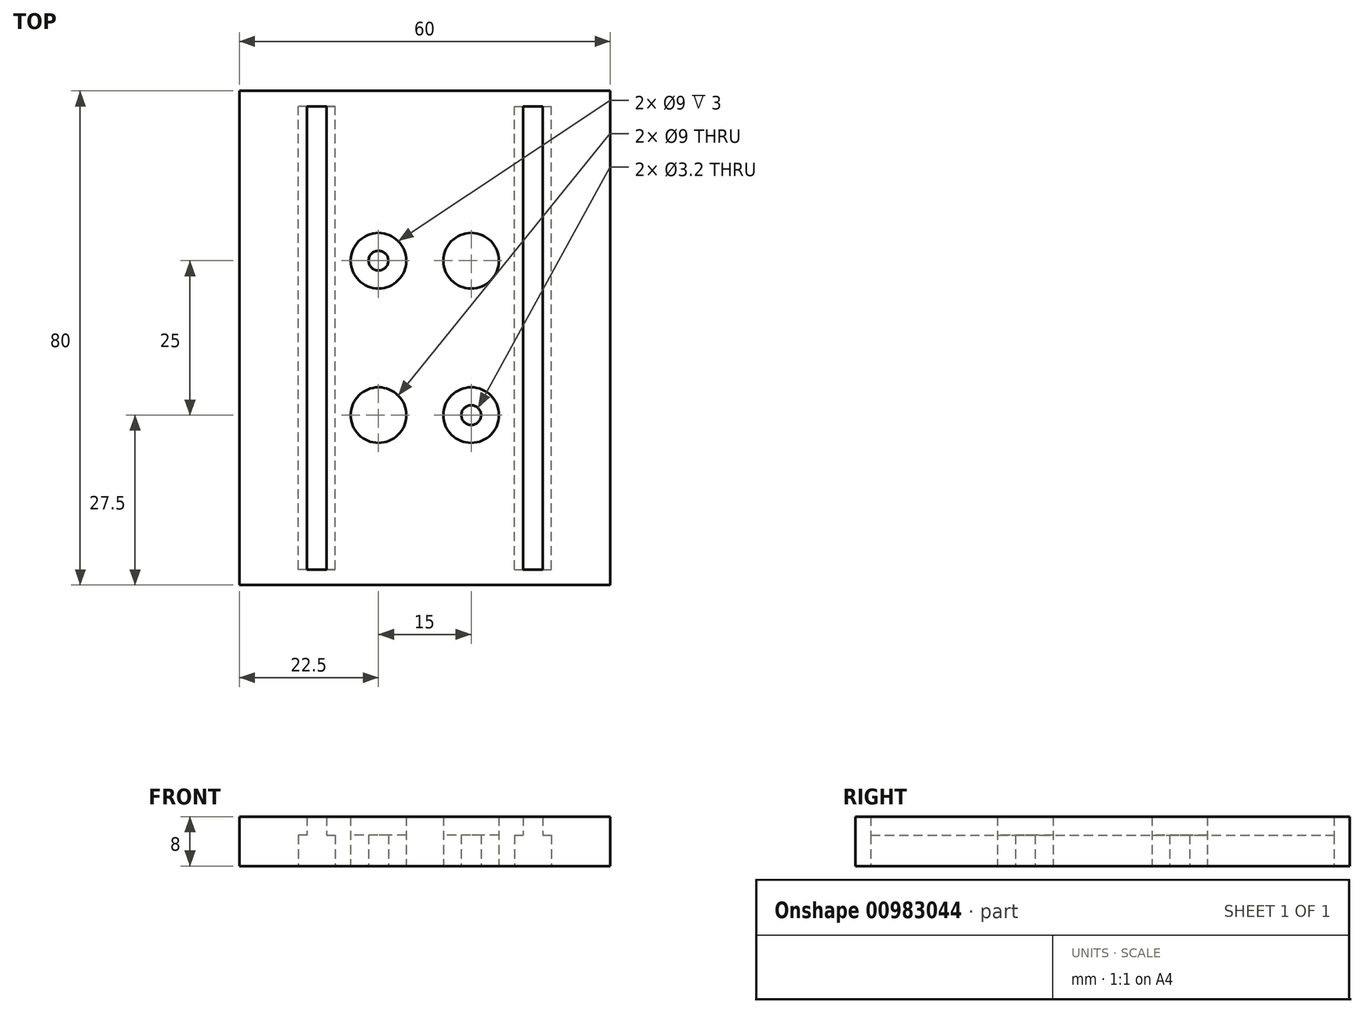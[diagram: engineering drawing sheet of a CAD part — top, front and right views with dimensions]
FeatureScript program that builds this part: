
annotation { "Feature Type Name" : "Feature", "Feature Type Description" : "" }
export const myFeature = defineFeature(function(context is Context, id is Id, definition is map)
    precondition{}
    {
        {
            var Q0;
            Q0=qCreatedBy(makeId("Top.planeOp"),FACE);
            var sketch = newSketch(context, id + "F0", { "sketchPlane" : qUnion([Q0])});
            skLineSegment(sketch, "E0.bottom", {"start": v(-30, 40) * mm, "end": v(30, 40) * mm});
            skLineSegment(sketch, "E0.top", {"start": v(-30, -40) * mm, "end": v(30, -40) * mm});
            skLineSegment(sketch, "E0.left", {"start": v(-30, 40) * mm, "end": v(-30, -40) * mm});
            skLineSegment(sketch, "E0.right", {"start": v(30, 40) * mm, "end": v(30, -40) * mm});
            skPoint(sketch, "E0.middle", {"position": v(0, 0) * mm});
            skLineSegment(sketch, "E1.bottom", {"start": v(-7.5, 12.5) * mm, "end": v(7.5, 12.5) * mm, "construction": true});
            skLineSegment(sketch, "E1.top", {"start": v(-7.5, -12.5) * mm, "end": v(7.5, -12.5) * mm, "construction": true});
            skLineSegment(sketch, "E1.left", {"start": v(-7.5, 12.5) * mm, "end": v(-7.5, -12.5) * mm, "construction": true});
            skLineSegment(sketch, "E1.right", {"start": v(7.5, 12.5) * mm, "end": v(7.5, -12.5) * mm, "construction": true});
            skCircle(sketch, "E2", {"center": v(-7.5, 12.5) * mm, "radius": 4.5 * mm});
            skCircle(sketch, "E3", {"center": v(-7.5, 12.5) * mm, "radius": 1.6 * mm});
            skCircle(sketch, "E4.MirrorC", {"center": v(-7.5, -12.5) * mm, "radius": 4.5 * mm});
            skCircle(sketch, "E5.MirrorC", {"center": v(-7.5, -12.5) * mm, "radius": 1.6 * mm});
            skCircle(sketch, "E6.MirrorC", {"center": v(7.5, 12.5) * mm, "radius": 4.5 * mm});
            skCircle(sketch, "E7.MirrorC", {"center": v(7.5, 12.5) * mm, "radius": 1.6 * mm});
            skCircle(sketch, "E8.MirrorC", {"center": v(7.5, -12.5) * mm, "radius": 4.5 * mm});
            skCircle(sketch, "E9.MirrorC", {"center": v(7.5, -12.5) * mm, "radius": 1.6 * mm});
            skSolve(sketch);
        }
        {
            var Q0;
            Q0=makeQuery(id+"F0.imprint","IMPRINT",FACE,{"disambiguationData":[TD([[makeQuery(id+"F0.imprint","IMPRINT",EDGE,{"derivedFrom":sQuery(id+"F0.wireOp",EDGE,"E0.bottom")}),-1.0]])]});
            extrude(context, id + "F1", {"entities" : qUnion([Q0]), "depth" : 8 * mm, "offsetDistance" : 25 * mm});
        }
        {
            var Q0;
            Q0=makeQuery(id+"F0.imprint","IMPRINT",FACE,{"disambiguationData":[TD([[makeQuery(id+"F0.imprint","IMPRINT",EDGE,{"derivedFrom":sQuery(id+"F0.wireOp",EDGE,"E2")}),1.0]])]});
            var Q1;
            Q1=makeQuery(id+"F0.imprint","IMPRINT",FACE,{"disambiguationData":[TD([[makeQuery(id+"F0.imprint","IMPRINT",EDGE,{"derivedFrom":sQuery(id+"F0.wireOp",EDGE,"E4.MirrorC")}),-1.0]])]});
            var Q2;
            Q2=makeQuery(id+"F0.imprint","IMPRINT",FACE,{"disambiguationData":[TD([[makeQuery(id+"F0.imprint","IMPRINT",EDGE,{"derivedFrom":sQuery(id+"F0.wireOp",EDGE,"E8.MirrorC")}),1.0]])]});
            var Q3;
            Q3=makeQuery(id+"F0.imprint","IMPRINT",FACE,{"disambiguationData":[TD([[makeQuery(id+"F0.imprint","IMPRINT",EDGE,{"derivedFrom":sQuery(id+"F0.wireOp",EDGE,"E6.MirrorC")}),-1.0]])]});
            extrude(context, id + "F2", {"entities" : qUnion([Q0, Q1, Q2, Q3]), "operationType" : NewBodyOperationType.ADD, "depth" : 5 * mm, "offsetDistance" : 25 * mm});
        }
        {
            var Q0;
            {var subQ0=sQuery(id+"F0.wireOp",EDGE,"E8.MirrorC");var subQ1=sQuery(id+"F0.wireOp",EDGE,"E6.MirrorC");var subQ2=sQuery(id+"F0.wireOp",EDGE,"E4.MirrorC");var subQ3=sQuery(id+"F0.wireOp",EDGE,"E2");Q0=makeQuery(id+"F2.boolean.opBoolean","MERGE",FACE,{"derivedFrom":[makeQuery(id+"F1.opExtrude","CAP_FACE",FACE,{"disambiguationData":[OSD([sQuery(id+"F0.wireOp",EDGE,"E0.bottom"),sQuery(id+"F0.wireOp",EDGE,"E0.top"),sQuery(id+"F0.wireOp",EDGE,"E0.left"),sQuery(id+"F0.wireOp",EDGE,"E0.right"),subQ3,subQ2,subQ1,subQ0])],"isStart":true}),makeQuery(id+"F2.opExtrude","CAP_FACE",FACE,{"disambiguationData":[OSD([subQ3,sQuery(id+"F0.wireOp",EDGE,"E3")])],"isStart":true}),makeQuery(id+"F2.opExtrude","CAP_FACE",FACE,{"disambiguationData":[OSD([subQ2,sQuery(id+"F0.wireOp",EDGE,"E5.MirrorC")])],"isStart":true}),makeQuery(id+"F2.opExtrude","CAP_FACE",FACE,{"disambiguationData":[OSD([subQ1,sQuery(id+"F0.wireOp",EDGE,"E7.MirrorC")])],"isStart":true}),makeQuery(id+"F2.opExtrude","CAP_FACE",FACE,{"disambiguationData":[OSD([subQ0,sQuery(id+"F0.wireOp",EDGE,"E9.MirrorC")])],"isStart":true})]});}
            var sketch = newSketch(context, id + "F3", { "sketchPlane" : qUnion([Q0])});
            skLineSegment(sketch, "E10.bottom", {"start": v(17.5, -37.5) * mm, "end": v(-17.5, -37.5) * mm, "construction": true});
            skLineSegment(sketch, "E10.top", {"start": v(17.5, 37.5) * mm, "end": v(-17.5, 37.5) * mm, "construction": true});
            skLineSegment(sketch, "E10.left", {"start": v(17.5, -37.5) * mm, "end": v(17.5, 37.5) * mm, "construction": true});
            skLineSegment(sketch, "E10.right", {"start": v(-17.5, -37.5) * mm, "end": v(-17.5, 37.5) * mm, "construction": true});
            skPoint(sketch, "E10.middle", {"position": v(0, 0) * mm});
            skLineSegment(sketch, "E11.bottom", {"start": v(-17.5, 37.5) * mm, "end": v(-20.5, 37.5) * mm});
            skLineSegment(sketch, "E11.top", {"start": v(-17.5, -37.5) * mm, "end": v(-20.5, -37.5) * mm});
            skLineSegment(sketch, "E11.left", {"start": v(-17.5, 37.5) * mm, "end": v(-17.5, -37.5) * mm});
            skLineSegment(sketch, "E11.right", {"start": v(-20.5, 37.5) * mm, "end": v(-20.5, -37.5) * mm});
            skLineSegment(sketch, "E12.bottom", {"start": v(-17.5, 37.5) * mm, "end": v(-15.9, 37.5) * mm});
            skLineSegment(sketch, "E12.top", {"start": v(-17.5, -37.5) * mm, "end": v(-15.9, -37.5) * mm});
            skLineSegment(sketch, "E12.right", {"start": v(-15.9, 37.5) * mm, "end": v(-15.9, -37.5) * mm});
            skLineSegment(sketch, "E13.MirrorCS", {"start": v(-19.1, 37.5) * mm, "end": v(-19.1, -37.5) * mm});
            skLineSegment(sketch, "E14.MirrorCS", {"start": v(-14.5, 37.5) * mm, "end": v(-14.5, -37.5) * mm});
            skLineSegment(sketch, "E15.MirrorCS", {"start": v(14.5, 37.5) * mm, "end": v(14.5, -37.5) * mm});
            skLineSegment(sketch, "E16.MirrorCS", {"start": v(15.9, 37.5) * mm, "end": v(15.9, -37.5) * mm});
            skLineSegment(sketch, "E17.MirrorCS", {"start": v(19.1, 37.5) * mm, "end": v(19.1, -37.5) * mm});
            skLineSegment(sketch, "E18.MirrorCS", {"start": v(20.5, 37.5) * mm, "end": v(20.5, -37.5) * mm});
            skLineSegment(sketch, "E19", {"start": v(-20.5, 37.5) * mm, "end": v(-14.5, 37.5) * mm});
            skLineSegment(sketch, "E20", {"start": v(14.5, 37.5) * mm, "end": v(20.5, 37.5) * mm});
            skLineSegment(sketch, "E21", {"start": v(14.5, -37.5) * mm, "end": v(20.5, -37.5) * mm});
            skLineSegment(sketch, "E22", {"start": v(-20.5, -37.5) * mm, "end": v(-14.5, -37.5) * mm});
            skSolve(sketch);
        }
        {
            var Q0;
            {var subQ0=sQuery(id+"F3.wireOp",EDGE,"E11.right");Q0=makeQuery(id+"F3.imprint","IMPRINT",FACE,{"disambiguationData":[TD([[makeQuery(id+"F3.imprint","IMPRINT",EDGE,{"derivedFrom":subQ0}),1.0]])]});}
            var Q1;
            Q1=makeQuery(id+"F3.imprint","IMPRINT",FACE,{"disambiguationData":[TD([[makeQuery(id+"F3.imprint","IMPRINT",EDGE,{"derivedFrom":sQuery(id+"F3.wireOp",EDGE,"E12.right")}),1.0]])]});
            var Q2;
            {var subQ0=sQuery(id+"F3.wireOp",EDGE,"E15.MirrorCS");Q2=makeQuery(id+"F3.imprint","IMPRINT",FACE,{"disambiguationData":[TD([[makeQuery(id+"F3.imprint","IMPRINT",EDGE,{"derivedFrom":subQ0}),1.0]])]});}
            var Q3;
            {var subQ0=sQuery(id+"F3.wireOp",EDGE,"E17.MirrorCS");Q3=makeQuery(id+"F3.imprint","IMPRINT",FACE,{"disambiguationData":[TD([[makeQuery(id+"F3.imprint","IMPRINT",EDGE,{"derivedFrom":subQ0}),1.0]])]});}
            extrude(context, id + "F4", {"entities" : qUnion([Q0, Q1, Q2, Q3]), "operationType" : NewBodyOperationType.REMOVE, "depth" : -5 * mm, "offsetDistance" : 25 * mm});
        }
        {
            var Q0;
            {var subQ0=sQuery(id+"F3.wireOp",EDGE,"E11.left");Q0=makeQuery(id+"F3.imprint","IMPRINT",FACE,{"disambiguationData":[TD([[makeQuery(id+"F3.imprint","IMPRINT",EDGE,{"derivedFrom":subQ0}),-1.0]])]});}
            var Q1;
            Q1=makeQuery(id+"F3.imprint","IMPRINT",FACE,{"disambiguationData":[TD([[makeQuery(id+"F3.imprint","IMPRINT",EDGE,{"derivedFrom":sQuery(id+"F3.wireOp",EDGE,"E11.left")}),1.0]])]});
            var Q2;
            {var subQ0=sQuery(id+"F3.wireOp",EDGE,"E16.MirrorCS");Q2=makeQuery(id+"F3.imprint","IMPRINT",FACE,{"disambiguationData":[TD([[makeQuery(id+"F3.imprint","IMPRINT",EDGE,{"derivedFrom":subQ0}),1.0]])]});}
            extrude(context, id + "F5", {"entities" : qUnion([Q0, Q1, Q2]), "operationType" : NewBodyOperationType.REMOVE, "oppositeDirection" : true, "depth" : 25 * mm, "offsetDistance" : 25 * mm});
        }
    });
